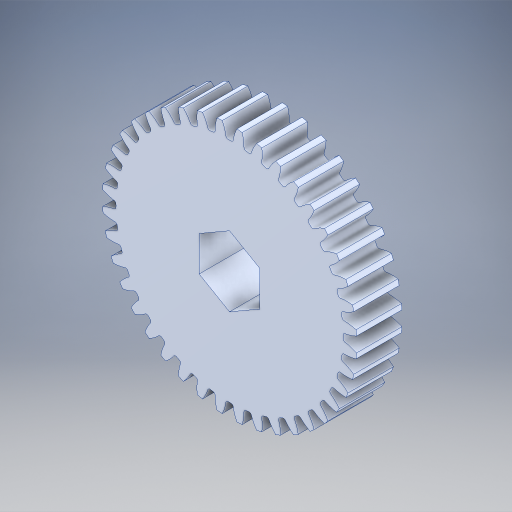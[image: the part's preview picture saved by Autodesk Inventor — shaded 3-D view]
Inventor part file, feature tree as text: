
AUTODESK INVENTOR PART (.ipt)
format: ipt  version: 2024 (Build 280153000, 153)  size: 887,296 bytes
history: native  units: in
note: dims shown in document units (in); Inventor stores cm internally (conversion verified against a paired STEP export)
features: extrude x1, sketch x1, boolean_combine x1
ambient origin geometry x8: Origin, YZ Plane, XZ Plane, XY Plane, X Axis, Y Axis, Z Axis, Center Point
bodies: Solid1 (feature_tree)
feature tree (3):
  extrude  "Extrusion1"  [1 undecoded]
  sketch  "Sketch1"  dims[d0=0.0in d1=0.0in]
  boolean_combine  "Combine1"
note: 1 required parameter value undecoded (feature->parameter linkage not recoverable at this tier; creation-order binding heuristic only, values carry confidence <= 0.55)
